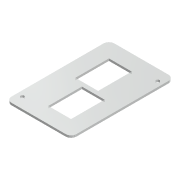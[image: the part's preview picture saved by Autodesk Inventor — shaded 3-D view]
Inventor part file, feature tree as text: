
AUTODESK INVENTOR PART (.ipt)
format: ipt  version: 2016 SP2 (Build 200236200, 236)  size: 123,904 bytes
history: native  units: mm
features: sketch x2, extrude x1, hole x1, fillet x1
ambient origin geometry x8: Origin, YZ Plane, XZ Plane, XY Plane, X Axis, Y Axis, Z Axis, Center Point
bodies: Body1 (feature_tree)
feature tree (5):
  extrude  "Extrusion3"  Depth=95.0mm
  hole  "Hole1"  [1 undecoded]
  fillet  "Fillet1"  Radius=31.0mm
  sketch  "Sketch1"  dims[d4=2.0mm d5=0.0mm]
  sketch  "Sketch2"  dims[d6=3.2mm d7=6.0mm d8=4.0mm d9=2.0mm d10=90.0deg d11=8.0mm d12=20.594885mm d13=95.0mm d14=60.0mm d15=31.0mm d16=21.0mm d17=5.0mm d18=17.5mm d19=17.5mm d20=5.0mm d21=75.0mm d22=50.0mm d23=5.0mm]
note: 1 required parameter value undecoded (feature->parameter linkage not recoverable at this tier; creation-order binding heuristic only, values carry confidence <= 0.55)
